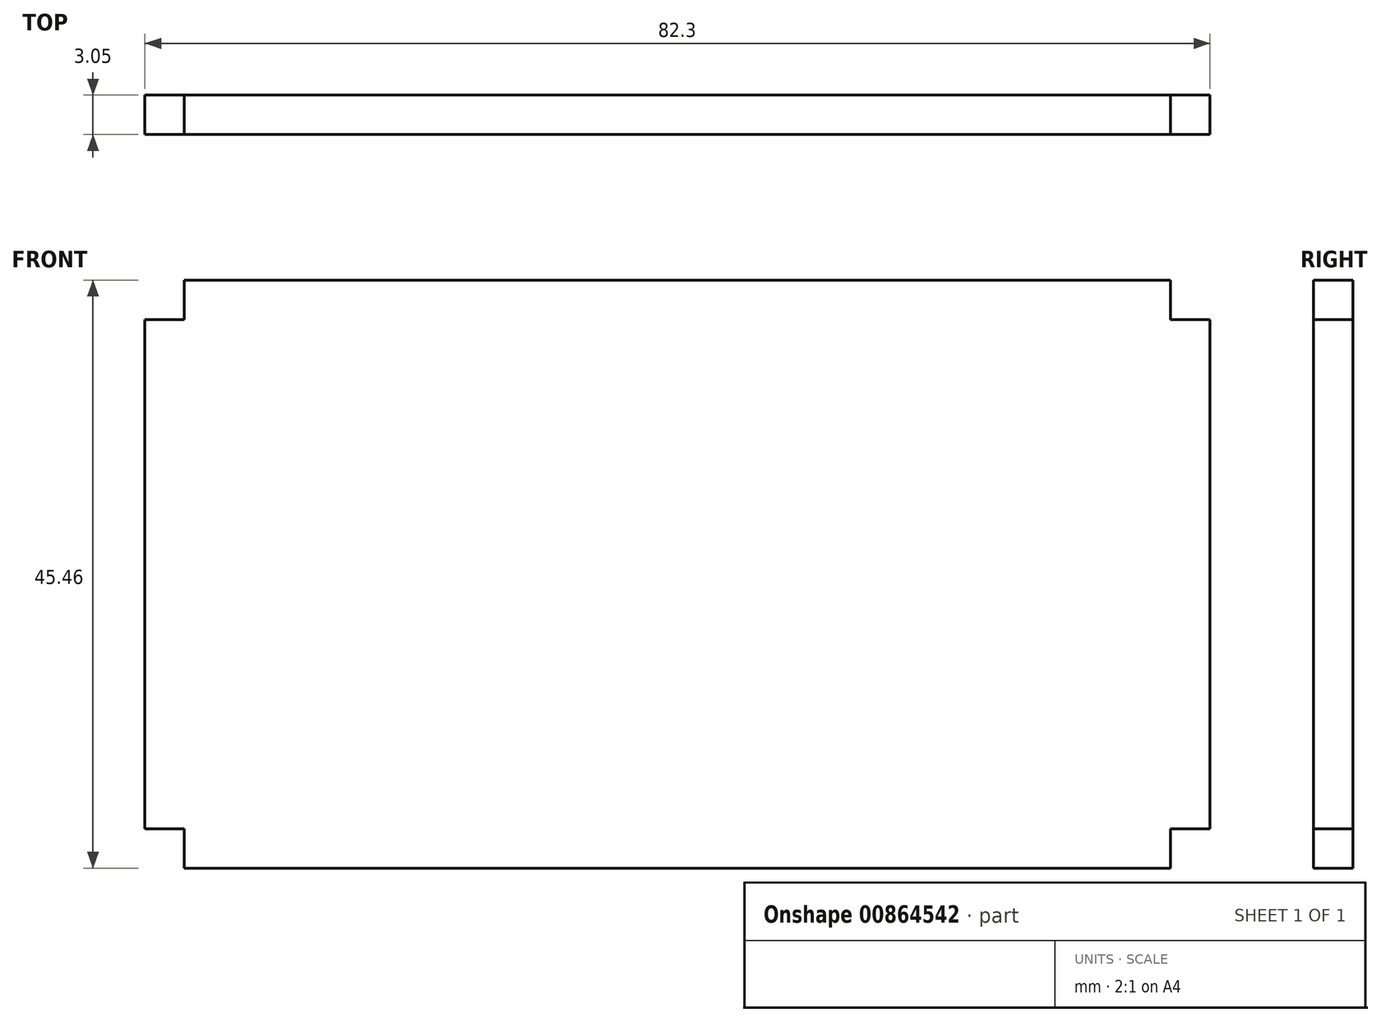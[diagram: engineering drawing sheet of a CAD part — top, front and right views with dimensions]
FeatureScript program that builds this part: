
annotation { "Feature Type Name" : "Feature", "Feature Type Description" : "" }
export const myFeature = defineFeature(function(context is Context, id is Id, definition is map)
    precondition{}
    {
        {
            var Q0;
            Q0=qCreatedBy(makeId("Front.planeOp"),FACE);
            var sketch = newSketch(context, id + "F0", { "sketchPlane" : qUnion([Q0])});
            skLineSegment(sketch, "E0", {"start": v(-38.1, 22.73) * mm, "end": v(38.1, 22.73) * mm});
            skLineSegment(sketch, "E1", {"start": v(38.1, 22.73) * mm, "end": v(38.1, 19.69) * mm});
            skLineSegment(sketch, "E2", {"start": v(38.1, 19.69) * mm, "end": v(41.15, 19.69) * mm});
            skLineSegment(sketch, "E3", {"start": v(41.15, 19.69) * mm, "end": v(41.15, -19.69) * mm});
            skLineSegment(sketch, "E4", {"start": v(41.15, -19.68) * mm, "end": v(38.1, -19.68) * mm});
            skLineSegment(sketch, "E5", {"start": v(38.1, -19.68) * mm, "end": v(38.1, -22.73) * mm});
            skLineSegment(sketch, "E6", {"start": v(38.1, -22.73) * mm, "end": v(-38.1, -22.73) * mm});
            skLineSegment(sketch, "E7", {"start": v(-38.1, -22.73) * mm, "end": v(-38.1, -19.69) * mm});
            skLineSegment(sketch, "E8", {"start": v(-38.1, -19.69) * mm, "end": v(-41.15, -19.69) * mm});
            skLineSegment(sketch, "E9", {"start": v(-41.15, -19.69) * mm, "end": v(-41.15, 19.69) * mm});
            skLineSegment(sketch, "E10", {"start": v(-41.15, 19.69) * mm, "end": v(-38.1, 19.69) * mm});
            skLineSegment(sketch, "E11", {"start": v(-38.1, 19.69) * mm, "end": v(-38.1, 22.73) * mm});
            skSolve(sketch);
        }
        {
            var Q0;
            Q0 = qSketchRegion(id + "F0", true);
            extrude(context, id + "F1", {"entities" : qUnion([Q0]), "depth" : 3.05 * mm, "offsetDistance" : 25.4 * mm});
        }
    });
